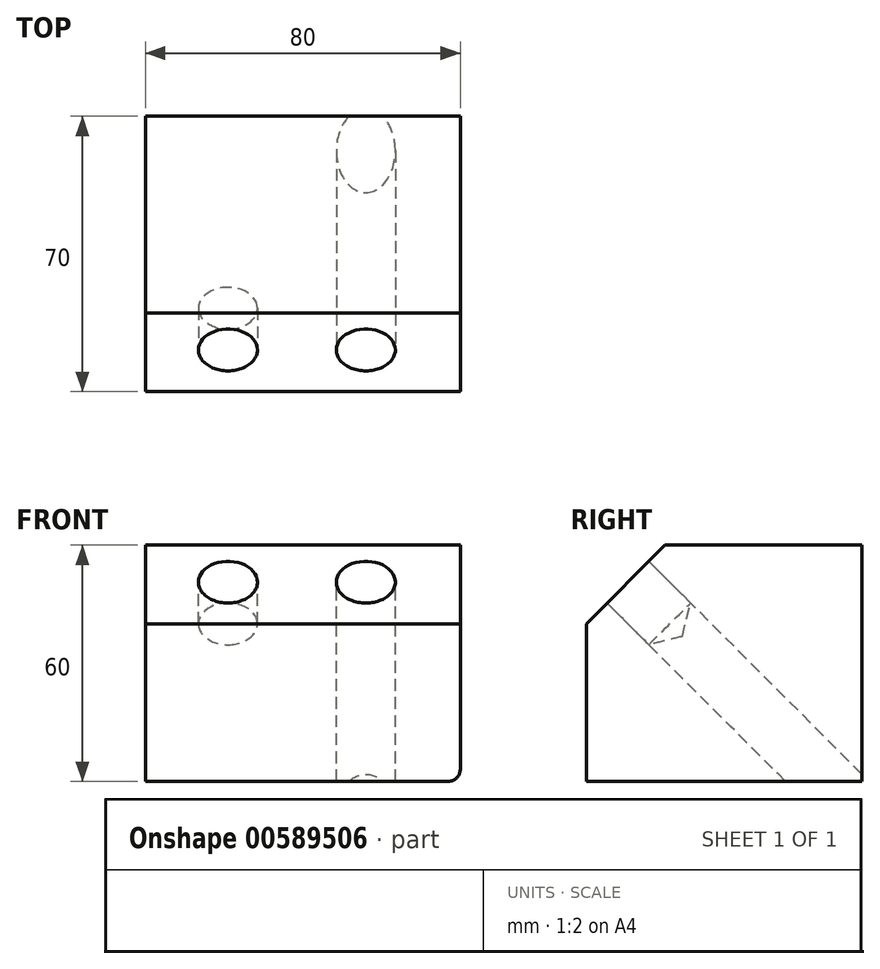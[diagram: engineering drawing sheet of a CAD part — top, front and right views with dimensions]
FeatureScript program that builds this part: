
annotation { "Feature Type Name" : "Feature", "Feature Type Description" : "" }
export const myFeature = defineFeature(function(context is Context, id is Id, definition is map)
    precondition{}
    {
        {
            var Q0;
            Q0=qCreatedBy(makeId("Top.planeOp"),FACE);
            var sketch = newSketch(context, id + "F0", { "sketchPlane" : qUnion([Q0])});
            skLineSegment(sketch, "E0.bottom", {"start": v(-80, -70) * mm, "end": v(0, -70) * mm});
            skLineSegment(sketch, "E0.top", {"start": v(-80, 0) * mm, "end": v(0, 0) * mm});
            skLineSegment(sketch, "E0.left", {"start": v(-80, -70) * mm, "end": v(-80, 0) * mm});
            skLineSegment(sketch, "E0.right", {"start": v(0, -70) * mm, "end": v(0, 0) * mm});
            skSolve(sketch);
        }
        {
            var Q0;
            Q0 = qSketchRegion(id + "F0", true);
            extrude(context, id + "F1", {"entities" : qUnion([Q0]), "depth" : 60 * mm, "offsetDistance" : 25 * mm});
        }
        {
            var Q0;
            Q0=makeQuery(id+"F1.opExtrude","CAP_EDGE",EDGE,{"disambiguationData":[OSD([sQuery(id+"F0.wireOp",EDGE,"E0.bottom")])],"isStart":false});
            chamfer(context, id + "F2", {"entities" : qUnion([Q0]), "width" : 20 * mm, "tangentPropagation" : true});
        }
        {
            var Q0;
            Q0=makeQuery(id+"F2.opChamfer","BLEND_FACE",FACE,{"disambiguationData":[OSD([sQuery(id+"F0.wireOp",EDGE,"E0.bottom")])]});
            var sketch = newSketch(context, id + "F3", { "sketchPlane" : qUnion([Q0])});
            skPoint(sketch, "E1", {"position": v(-24, -6.21) * mm});
            skSolve(sketch);
        }
        {
            var Q0;
            Q0=sQuery(id+"F3.wireOp",VERTEX,"E1");
            var Q1;
            Q1=makeQuery(id+"F1.opExtrude","SWEPT_BODY",BODY,{"disambiguationData":[OSD([sQuery(id+"F0.wireOp",EDGE,"E0.bottom"),sQuery(id+"F0.wireOp",EDGE,"E0.top"),sQuery(id+"F0.wireOp",EDGE,"E0.left"),sQuery(id+"F0.wireOp",EDGE,"E0.right")])]});
            hole(context, id + "F4", {"style" : HoleStyle.SIMPLE, "endStyle" : HoleEndStyle.THROUGH, "holeDiameter" : 15 * mm, "majorDiameter" : 16 * mm, "isTappedThrough" : true, "tappedDepth" : 12 * mm, "tapClearance" : 3, "locations" : qUnion([Q0]), "scope" : qUnion([Q1])});
        }
        {
            var Q0;
            Q0=makeQuery(id+"F2.opChamfer","BLEND_FACE",FACE,{"disambiguationData":[OSD([sQuery(id+"F0.wireOp",EDGE,"E0.bottom")])]});
            var sketch = newSketch(context, id + "F5", { "sketchPlane" : qUnion([Q0])});
            skPoint(sketch, "E2", {"position": v(-59.02, -6.21) * mm});
            skSolve(sketch);
        }
        {
            var Q0;
            Q0=sQuery(id+"F5.wireOp",VERTEX,"E2");
            var Q1;
            Q1=makeQuery(id+"F1.opExtrude","SWEPT_BODY",BODY,{"disambiguationData":[OSD([sQuery(id+"F0.wireOp",EDGE,"E0.bottom"),sQuery(id+"F0.wireOp",EDGE,"E0.top"),sQuery(id+"F0.wireOp",EDGE,"E0.left"),sQuery(id+"F0.wireOp",EDGE,"E0.right")])]});
            hole(context, id + "F6", {"style" : HoleStyle.SIMPLE, "endStyle" : HoleEndStyle.BLIND, "holeDiameter" : 15 * mm, "majorDiameter" : 5 * mm, "holeDepth" : 15 * mm, "isTappedThrough" : true, "tappedDepth" : 12 * mm, "tapClearance" : 3, "locations" : qUnion([Q0]), "scope" : qUnion([Q1])});
        }
        {
            var Q0;
            Q0=makeQuery(id+"F1.opExtrude","CAP_EDGE",EDGE,{"disambiguationData":[OSD([sQuery(id+"F0.wireOp",EDGE,"E0.right")])],"isStart":true});
            fillet(context, id + "F7", {"entities" : qUnion([Q0]), "radius" : 3 * mm, "tangentPropagation" : true, "allowEdgeOverflow" : false});
        }
    });
